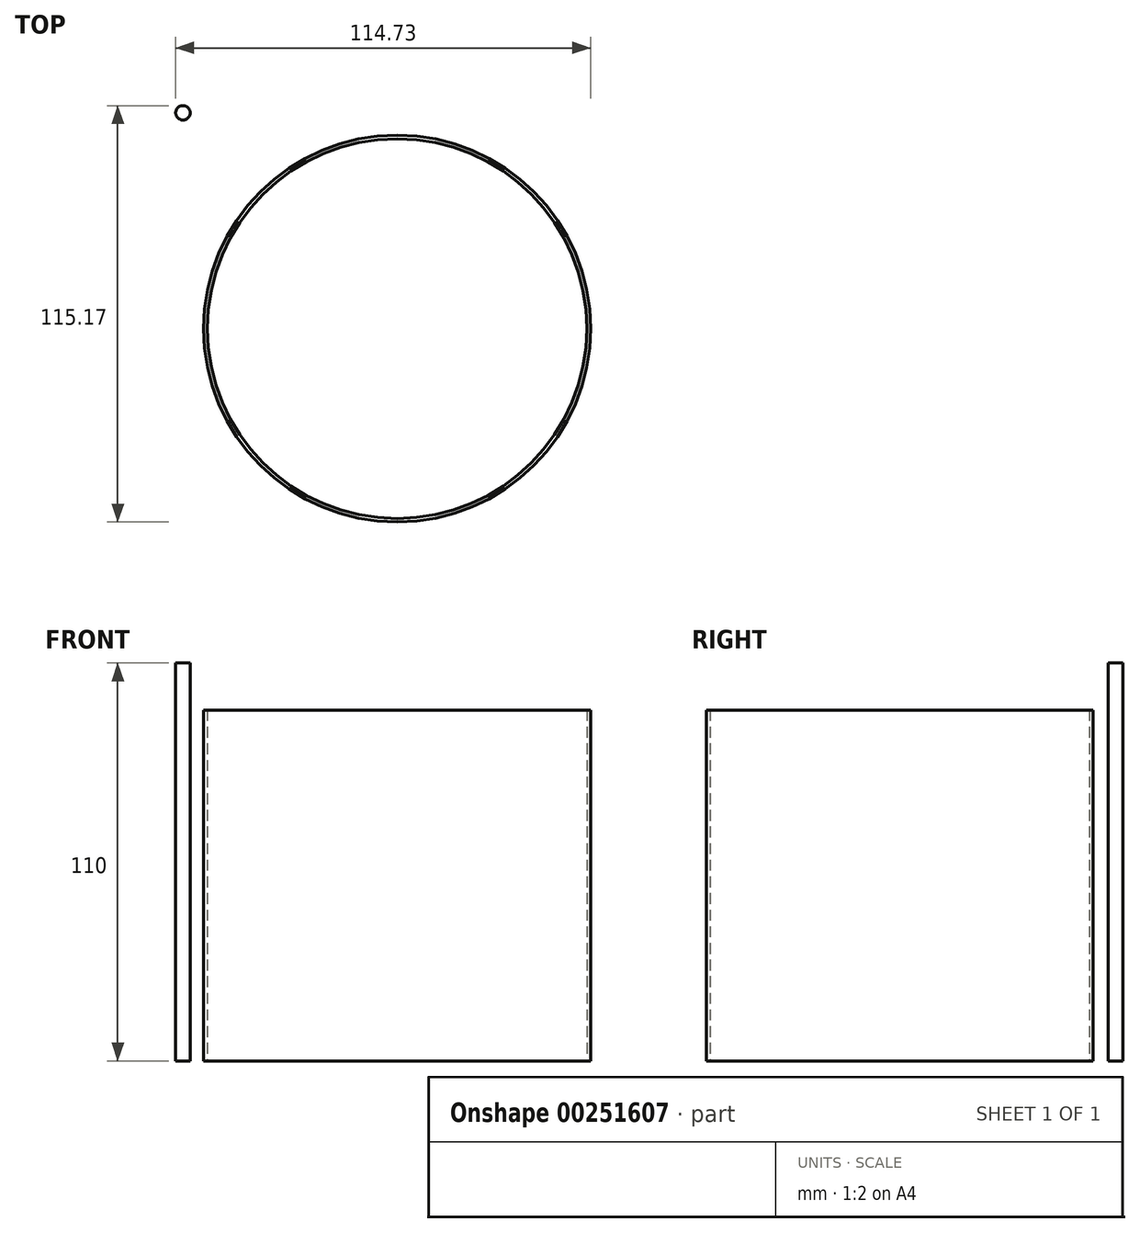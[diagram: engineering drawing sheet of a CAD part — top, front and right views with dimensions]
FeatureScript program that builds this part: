
annotation { "Feature Type Name" : "Feature", "Feature Type Description" : "" }
export const myFeature = defineFeature(function(context is Context, id is Id, definition is map)
    precondition{}
    {
        {
            var Q0;
            Q0=qCreatedBy(makeId("Top.planeOp"),FACE);
            var sketch = newSketch(context, id + "F0", { "sketchPlane" : qUnion([Q0])});
            skCircle(sketch, "E0", {"center": v(0, 0) * mm, "radius": 53.5 * mm});
            skSolve(sketch);
        }
        {
            var Q0;
            Q0=makeQuery(id+"F0.imprint","IMPRINT",FACE,{"disambiguationData":[TD([[makeQuery(id+"F0.imprint","IMPRINT",EDGE,{"derivedFrom":sQuery(id+"F0.wireOp",EDGE,"E0")}),1.0]])]});
            extrude(context, id + "F1", {"entities" : qUnion([Q0]), "depth" : 97 * mm});
        }
        {
            var Q0;
            Q0=makeQuery(id+"F1.opExtrude","CAP_FACE",FACE,{"disambiguationData":[OSD([sQuery(id+"F0.wireOp",EDGE,"E0")])],"isStart":false});
            shell(context, id + "F2", {"entities" : qUnion([Q0]), "thickness" : 1 * mm});
        }
        {
            var Q0;
            {var subQ0=sQuery(id+"F0.wireOp",EDGE,"E0");Q0=makeQuery(id+"F2.opShell","OFFSET_FACE",FACE,{"disambiguationData":[OSD([subQ0]),TDD([makeQuery(id+"F1.opExtrude","CAP_FACE",FACE,{"disambiguationData":[OSD([subQ0])],"isStart":true})])]});}
            extrude(context, id + "F3", {"entities" : qUnion([Q0]), "operationType" : NewBodyOperationType.REMOVE, "endBound" : BoundingType.THROUGH_ALL, "oppositeDirection" : true, "depth" : 25 * mm});
        }
        {
            var Q0;
            Q0=qCreatedBy(makeId("Top.planeOp"),FACE);
            var sketch = newSketch(context, id + "F4", { "sketchPlane" : qUnion([Q0])});
            skCircle(sketch, "E1", {"center": v(-59.23, 59.67) * mm, "radius": 2 * mm});
            skSolve(sketch);
        }
        {
            var Q0;
            Q0=makeQuery(id+"F4.imprint","IMPRINT",FACE,{"disambiguationData":[TD([[makeQuery(id+"F4.imprint","IMPRINT",EDGE,{"derivedFrom":sQuery(id+"F4.wireOp",EDGE,"E1")}),1.0]])]});
            extrude(context, id + "F5", {"entities" : qUnion([Q0]), "depth" : 110 * mm});
        }
    });
